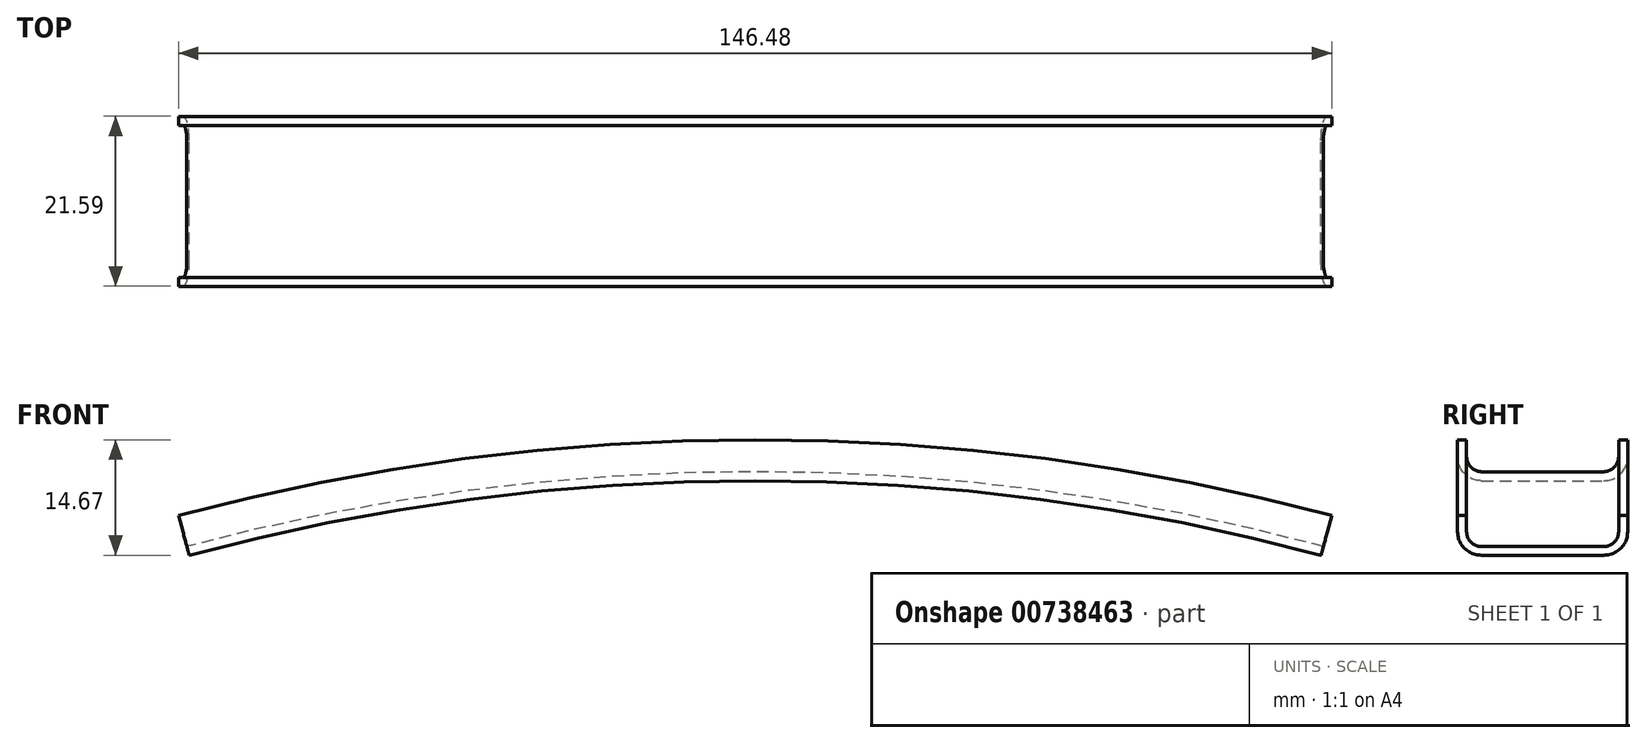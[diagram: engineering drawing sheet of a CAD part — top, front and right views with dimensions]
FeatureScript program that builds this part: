
annotation { "Feature Type Name" : "Feature", "Feature Type Description" : "" }
export const myFeature = defineFeature(function(context is Context, id is Id, definition is map)
    precondition{}
    {
        {
            var Q0;
            Q0=qCreatedBy(makeId("Right.planeOp"),FACE);
            cPlane(context, id + "F0", {"entities" : qUnion([Q0]), "cplaneType" : CPlaneType.OFFSET, "offset" : 4.78 / 50.8 * mm, "width" : 152.4 * mm, "height" : 152.4 * mm});
        }
        {
            var Q0;
            Q0=qCreatedBy(makeId("Right.planeOp"),FACE);
            var sketch = newSketch(context, id + "F1", { "sketchPlane" : qUnion([Q0])});
            skLineSegment(sketch, "E0", {"start": v(-7.75, 277.77) * mm, "end": v(7.75, 277.77) * mm});
            skLineSegment(sketch, "E1", {"start": v(0, 0) * mm, "end": v(0, 351.21) * mm, "construction": true});
            skLineSegment(sketch, "E2", {"start": v(-10.8, 280.82) * mm, "end": v(-10.8, 282.98) * mm});
            skLineSegment(sketch, "E3", {"start": v(10.8, 280.82) * mm, "end": v(10.8, 282.98) * mm});
            skPoint(sketch, "E4.visualSharp", {"position": v(10.8, 277.77) * mm});
            skArc(sketch, "E4.filletArc", {"start": v(7.75, 277.77) * mm, "mid": v(9.9, 278.67) * mm, "end": v(10.8, 280.82) * mm});
            skPoint(sketch, "E5.visualSharp", {"position": v(-10.8, 277.77) * mm});
            skArc(sketch, "E5.filletArc", {"start": v(-10.8, 280.82) * mm, "mid": v(-9.9, 278.67) * mm, "end": v(-7.75, 277.77) * mm});
            skLineSegment(sketch, "E6.0", {"start": v(9.65, 280.82) * mm, "end": v(9.65, 282.98) * mm});
            skLineSegment(sketch, "E6.1", {"start": v(-9.65, 280.82) * mm, "end": v(-9.65, 282.98) * mm});
            skArc(sketch, "E6.2", {"start": v(-9.65, 280.82) * mm, "mid": v(-9.1, 279.48) * mm, "end": v(-7.75, 278.92) * mm});
            skLineSegment(sketch, "E6.3", {"start": v(-7.75, 278.92) * mm, "end": v(7.75, 278.92) * mm});
            skArc(sketch, "E6.4", {"start": v(7.75, 278.92) * mm, "mid": v(9.1, 279.48) * mm, "end": v(9.65, 280.82) * mm});
            skLineSegment(sketch, "E7", {"start": v(-10.8, 282.98) * mm, "end": v(-9.65, 282.98) * mm});
            skLineSegment(sketch, "E8", {"start": v(9.65, 282.98) * mm, "end": v(10.8, 282.98) * mm});
            skSolve(sketch);
        }
        {
            var Q0;
            Q0=qCreatedBy(makeId("Top.planeOp"),FACE);
            var sketch = newSketch(context, id + "F2", { "sketchPlane" : qUnion([Q0])});
            skLineSegment(sketch, "E9", {"start": v(0, 0) * mm, "end": v(-186.93, 0) * mm, "construction": true});
            skLineSegment(sketch, "E10", {"start": v(0, 0) * mm, "end": v(0, -204.2) * mm, "construction": true});
            skLineSegment(sketch, "E11", {"start": v(0, -204.2) * mm, "end": v(0, -181.14) * mm, "construction": true});
            skSolve(sketch);
        }
        {
            var Q0;
            Q0=makeQuery(id+"F1.imprint","IMPRINT",FACE,{"disambiguationData":[TD([[makeQuery(id+"F1.imprint","IMPRINT",EDGE,{"derivedFrom":sQuery(id+"F1.wireOp",EDGE,"E0")}),1.0]])]});
            var Q1;
            Q1=sQuery(id+"F2.wireOp",EDGE,"E10");
            revolve(context, id + "F3", {"surfaceOperationType" : NewSurfaceOperationType.NEW, "entities" : qUnion([Q0]), "axis" : qUnion([Q1]), "revolveType" : RevolveType.SYMMETRIC, "angle" : 30 * degree});
        }
    });
